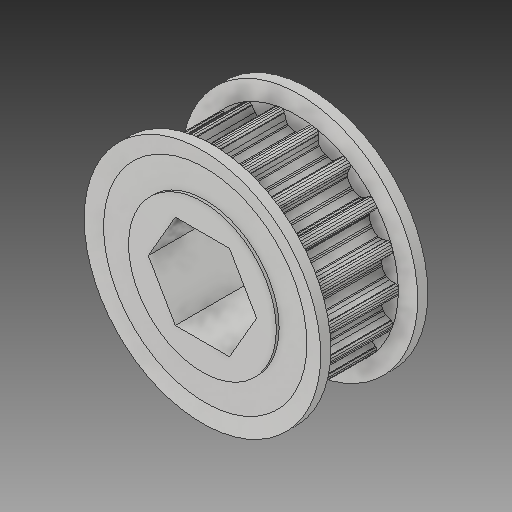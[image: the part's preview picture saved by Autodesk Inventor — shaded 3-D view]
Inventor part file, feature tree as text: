
AUTODESK INVENTOR PART (.ipt)
format: ipt  version: 2017 (Build 210142000, 142)  size: 549,376 bytes
history: native  units: in
note: dims shown in document units (in); Inventor stores cm internally (conversion verified against a paired STEP export)
features: mirror x1
ambient origin geometry x8: Origin, YZ Plane, XZ Plane, XY Plane, X Axis, Y Axis, Z Axis, Center Point
bodies: Solid1 (feature_tree)
feature tree (1):
  mirror  "Mirror1"
